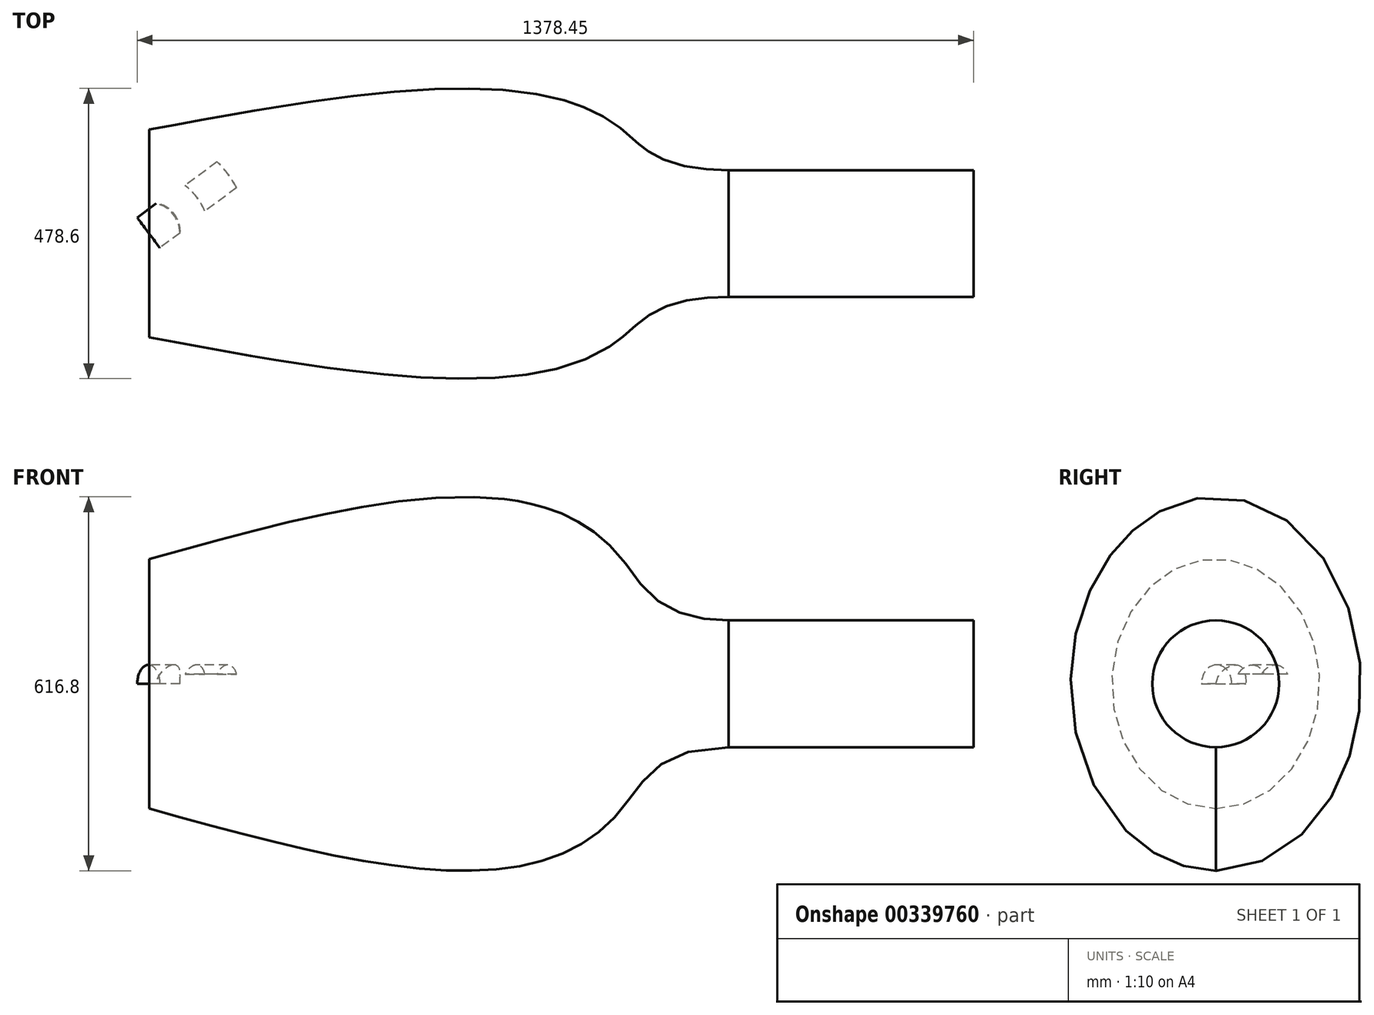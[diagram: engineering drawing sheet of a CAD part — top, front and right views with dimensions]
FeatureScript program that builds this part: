
annotation { "Feature Type Name" : "Feature", "Feature Type Description" : "" }
export const myFeature = defineFeature(function(context is Context, id is Id, definition is map)
    precondition{}
    {
        {
            var Q0;
            Q0=qCreatedBy(makeId("Top.planeOp"),FACE);
            var sketch = newSketch(context, id + "F0", { "sketchPlane" : qUnion([Q0])});
            skCircle(sketch, "E0", {"center": v(0, 0) * mm, "radius": 50.8 * mm});
            skSolve(sketch);
        }
        {
            var Q0;
            Q0=makeQuery(id+"F0.imprint","IMPRINT",FACE,{"disambiguationData":[TD([[makeQuery(id+"F0.imprint","IMPRINT",EDGE,{"derivedFrom":sQuery(id+"F0.wireOp",EDGE,"E0")}),1.0]])]});
            extrude(context, id + "F1", {"entities" : qUnion([Q0]), "depth" : 127 * mm, "hasDraft" : true, "draftAngle" : 3 * degree});
        }
        {
            var Q0;
            Q0=qCreatedBy(makeId("Right.planeOp"),FACE);
            var sketch = newSketch(context, id + "F2", { "sketchPlane" : qUnion([Q0])});
            skLineSegment(sketch, "E1.bottom", {"start": v(-162.85, 126) * mm, "end": v(-98.87, 126) * mm});
            skLineSegment(sketch, "E1.top", {"start": v(-162.85, 16.06) * mm, "end": v(-98.87, 16.06) * mm});
            skLineSegment(sketch, "E1.left", {"start": v(-162.85, 126) * mm, "end": v(-162.85, 16.06) * mm});
            skLineSegment(sketch, "E1.right", {"start": v(-98.87, 126) * mm, "end": v(-98.87, 16.06) * mm});
            skSolve(sketch);
        }
        {
            var Q0;
            Q0=makeQuery(id+"F2.imprint","IMPRINT",FACE,{"disambiguationData":[TD([[makeQuery(id+"F2.imprint","IMPRINT",EDGE,{"derivedFrom":sQuery(id+"F2.wireOp",EDGE,"E1.bottom")}),-1.0]])]});
            var Q1;
            Q1=makeQuery(id+"F1.opExtrude","SWEPT_FACE",FACE,{"disambiguationData":[OSD([sQuery(id+"F0.wireOp",EDGE,"E0")])]});
            revolve(context, id + "F3", {"entities" : qUnion([Q0]), "axis" : qUnion([Q1]), "revolveType" : RevolveType.FULL});
        }
        {
            var Q0;
            Q0=qCreatedBy(makeId("Top.planeOp"),FACE);
            var sketch = newSketch(context, id + "F4", { "sketchPlane" : qUnion([Q0])});
            skLineSegment(sketch, "E2", {"start": v(0, 0) * mm, "end": v(408.11, 302.5) * mm});
            skArc(sketch, "E3", {"start": v(629.78, 302.5) * mm, "mid": v(518.95, 339.1) * mm, "end": v(408.11, 302.5) * mm});
            skLineSegment(sketch, "E4", {"start": v(629.78, 302.5) * mm, "end": v(1037.9, 0) * mm});
            skSolve(sketch);
        }
        {
            var Q0;
            Q0=sQuery(id+"F4.wireOp",EDGE,"E4");
            var Q1;
            Q1=sQuery(id+"F4.wireOp",VERTEX,"E4.end");
            cPlane(context, id + "F5", {"entities" : qUnion([Q0, Q1]), "cplaneType" : CPlaneType.CURVE_POINT, "offset" : 25.4 * mm, "width" : 152.4 * mm, "height" : 152.4 * mm});
        }
        {
            var Q0;
            Q0=qCreatedBy(id+"F5.planeOp",FACE);
            var sketch = newSketch(context, id + "F6", { "sketchPlane" : qUnion([Q0])});
            skCircle(sketch, "E5", {"center": v(619.74, 0) * mm, "radius": 31.14 * mm});
            skSolve(sketch);
        }
        {
            var Q0;
            Q0=makeQuery(id+"F6.imprint","IMPRINT",FACE,{"disambiguationData":[TD([[makeQuery(id+"F6.imprint","IMPRINT",EDGE,{"derivedFrom":sQuery(id+"F6.wireOp",EDGE,"E5")}),1.0]])]});
            var Q1;
            Q1=sQuery(id+"F4.wireOp",EDGE,"E4");
            var Q2;
            Q2=sQuery(id+"F4.wireOp",EDGE,"E3");
            var Q3;
            Q3=sQuery(id+"F4.wireOp",EDGE,"E2");
            sweep(context, id + "F7", {"operationType" : NewBodyOperationType.INTERSECT, "profiles" : qUnion([Q0]), "path" : qUnion([Q1, Q2, Q3])});
        }
        {
            var Q0;
            Q0=qCreatedBy(makeId("Right.planeOp"),FACE);
            cPlane(context, id + "F8", {"entities" : qUnion([Q0]), "cplaneType" : CPlaneType.OFFSET, "offset" : 779.78 * mm, "width" : 152.4 * mm, "height" : 152.4 * mm});
        }
        {
            var Q0;
            Q0=qCreatedBy(id+"F8.planeOp",FACE);
            cPlane(context, id + "F9", {"entities" : qUnion([Q0]), "cplaneType" : CPlaneType.OFFSET, "offset" : 175.26 * mm, "width" : 152.4 * mm, "height" : 152.4 * mm});
        }
        {
            var Q0;
            Q0=qCreatedBy(id+"F9.planeOp",FACE);
            var sketch = newSketch(context, id + "F10", { "sketchPlane" : qUnion([Q0])});
            skCircle(sketch, "E6", {"center": v(0, 0) * mm, "radius": 104.59 * mm});
            skSolve(sketch);
        }
        {
            var Q0;
            Q0=qCreatedBy(id+"F8.planeOp",FACE);
            var sketch = newSketch(context, id + "F11", { "sketchPlane" : qUnion([Q0])});
            skEllipse(sketch, "E7", {"center": v(0, 0) * mm, "majorRadius": 171.45 * mm, "minorRadius": 205.74 * mm, "majorAxis": v(-1, 0)});
            skSolve(sketch);
        }
        {
            var Q0;
            Q0=qCreatedBy(makeId("Right.planeOp"),FACE);
            var sketch = newSketch(context, id + "F12", { "sketchPlane" : qUnion([Q0])});
            skEllipse(sketch, "E8.0.0", {"center": v(0, 0) * mm, "majorRadius": 205.74 * mm, "minorRadius": 171.45 * mm, "majorAxis": v(0, -1)});
            skSolve(sketch);
        }
        {
            var Q0;
            Q0 = qSketchRegion(id + "F10", true);
            extrude(context, id + "F13", {"entities" : qUnion([Q0]), "depth" : 403.86 * mm});
        }
        {
            var Q0;
            Q0=makeQuery(id+"F10.imprint","IMPRINT",FACE,{"disambiguationData":[TD([[makeQuery(id+"F10.imprint","IMPRINT",EDGE,{"derivedFrom":sQuery(id+"F10.wireOp",EDGE,"E6")}),1.0]])]});
            var Q1;
            Q1=makeQuery(id+"F11.imprint","IMPRINT",FACE,{"disambiguationData":[TD([[makeQuery(id+"F11.imprint","IMPRINT",EDGE,{"derivedFrom":sQuery(id+"F11.wireOp",EDGE,"E7")}),1.0]])]});
            var Q2;
            Q2=makeQuery(id+"F12.imprint","IMPRINT",FACE,{"disambiguationData":[TD([[makeQuery(id+"F12.imprint","IMPRINT",EDGE,{"derivedFrom":sQuery(id+"F12.wireOp",EDGE,"E8.0.0")}),1.0]])]});
            loft(context, id + "F14", {"startCondition" : LoftEndDerivativeType.NORMAL_TO_PROFILE, "startMagnitude" : 2, "sheetProfilesArray" : [{ "sheetProfileEntities" : qUnion([Q0]) }, { "sheetProfileEntities" : qUnion([Q1]) }, { "sheetProfileEntities" : qUnion([Q2]) }]});
        }
    });
